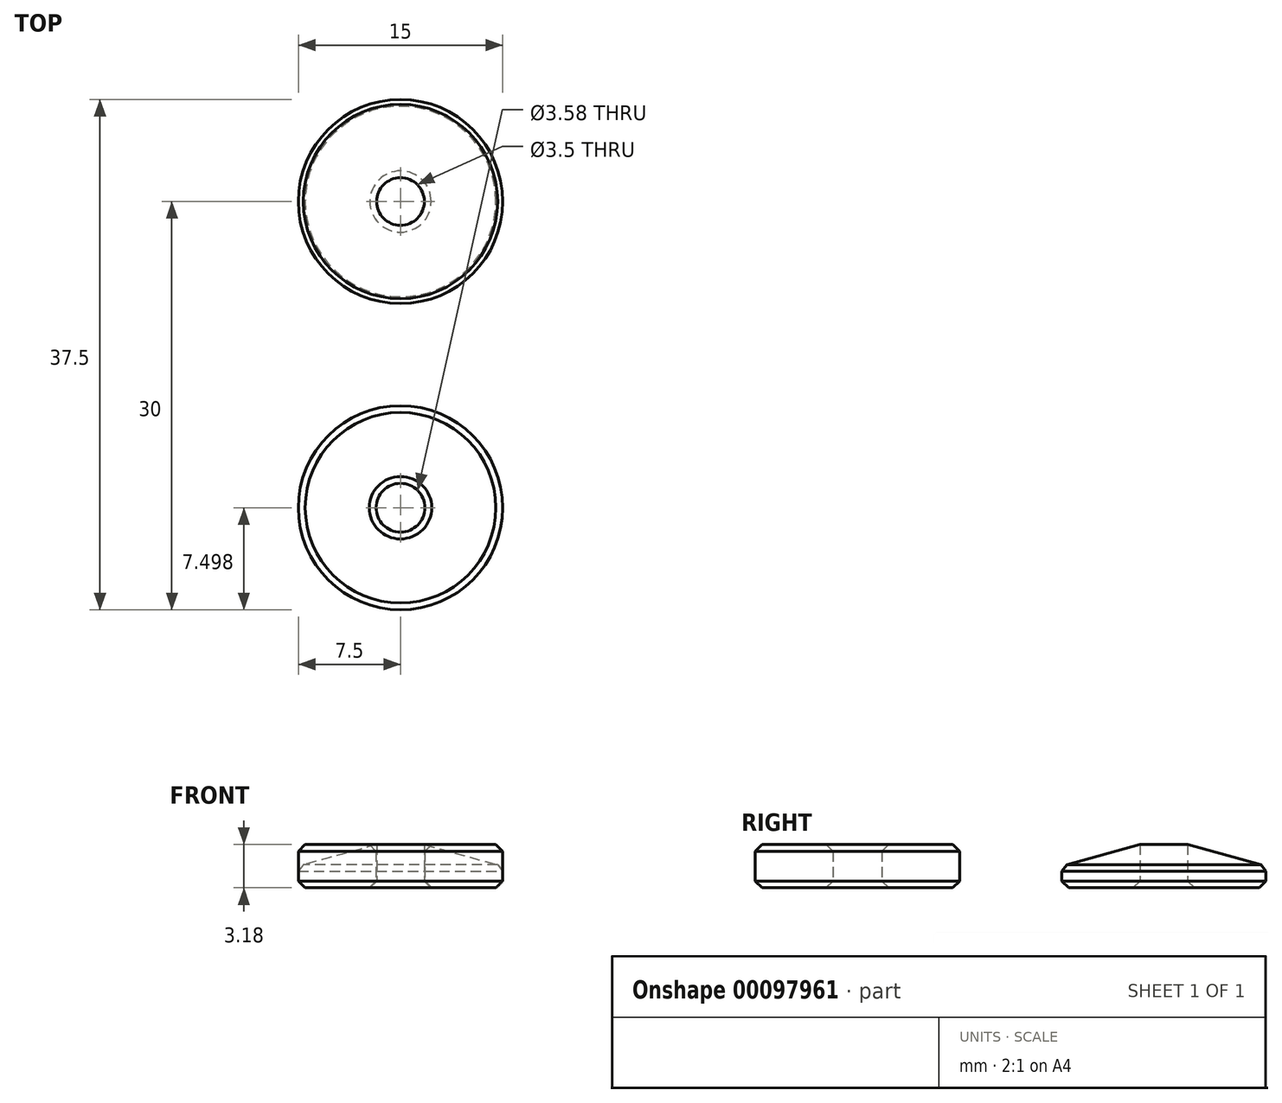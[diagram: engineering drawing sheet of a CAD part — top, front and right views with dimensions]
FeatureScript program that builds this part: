
annotation { "Feature Type Name" : "Feature", "Feature Type Description" : "" }
export const myFeature = defineFeature(function(context is Context, id is Id, definition is map)
    precondition{}
    {
        {
            var Q0;
            Q0=qCreatedBy(makeId("Top.planeOp"),FACE);
            var sketch = newSketch(context, id + "F0", { "sketchPlane" : qUnion([Q0])});
            skCircle(sketch, "E0", {"center": v(0, 0) * mm, "radius": 1.75 * mm});
            skCircle(sketch, "E1", {"center": v(0, 0) * mm, "radius": 7.5 * mm});
            skLineSegment(sketch, "E2", {"start": v(0, 0) * mm, "end": v(0, -22.5) * mm, "construction": true});
            skCircle(sketch, "E3", {"center": v(0, -22.5) * mm, "radius": 7.5 * mm});
            skCircle(sketch, "E4", {"center": v(0, -22.5) * mm, "radius": 1.8 * mm});
            skSolve(sketch);
        }
        {
            var Q0;
            Q0=makeQuery(id+"F0.imprint","IMPRINT",FACE,{"disambiguationData":[TD([[makeQuery(id+"F0.imprint","IMPRINT",EDGE,{"derivedFrom":sQuery(id+"F0.wireOp",EDGE,"E0")}),-1.0]])]});
            extrude(context, id + "F1", {"entities" : qUnion([Q0]), "depth" : 1.59 * mm});
        }
        {
            var Q0;
            Q0=qCreatedBy(makeId("Right.planeOp"),FACE);
            var sketch = newSketch(context, id + "F2", { "sketchPlane" : qUnion([Q0])});
            skLineSegment(sketch, "E5", {"start": v(0, 2.18) * mm, "end": v(0, 3.18) * mm, "construction": true});
            skLineSegment(sketch, "E6", {"start": v(1.75, 1.59) * mm, "end": v(1.75, 3.18) * mm});
            skLineSegment(sketch, "E7", {"start": v(1.75, 3.18) * mm, "end": v(7.5, 1.59) * mm});
            skLineSegment(sketch, "E8", {"start": v(7.5, 1.59) * mm, "end": v(1.75, 1.59) * mm});
            skSolve(sketch);
        }
        {
            var Q0;
            Q0=makeQuery(id+"F2.imprint","IMPRINT",FACE,{"disambiguationData":[TD([[makeQuery(id+"F2.imprint","IMPRINT",EDGE,{"derivedFrom":sQuery(id+"F2.wireOp",EDGE,"E6")}),-1.0]])]});
            var Q1;
            Q1=sQuery(id+"F2.wireOp",EDGE,"E5");
            revolve(context, id + "F3", {"operationType" : NewBodyOperationType.ADD, "entities" : qUnion([Q0]), "axis" : qUnion([Q1]), "revolveType" : RevolveType.FULL});
        }
        {
            var Q0;
            Q0=makeQuery(id+"F0.imprint","IMPRINT",FACE,{"disambiguationData":[TD([[makeQuery(id+"F0.imprint","IMPRINT",EDGE,{"derivedFrom":sQuery(id+"F0.wireOp",EDGE,"E3")}),1.0]])]});
            extrude(context, id + "F4", {"entities" : qUnion([Q0]), "depth" : 3.17 * mm});
        }
        {
            var Q0;
            Q0=makeQuery(id+"F1.opExtrude","CAP_EDGE",EDGE,{"disambiguationData":[OSD([sQuery(id+"F0.wireOp",EDGE,"E1")])],"isStart":true});
            var Q1;
            Q1=makeQuery(id+"F1.opExtrude","CAP_EDGE",EDGE,{"disambiguationData":[OSD([sQuery(id+"F0.wireOp",EDGE,"E0")])],"isStart":true});
            var Q2;
            Q2=makeQuery(id+"F4.opExtrude","CAP_EDGE",EDGE,{"disambiguationData":[OSD([sQuery(id+"F0.wireOp",EDGE,"E3")])],"isStart":false});
            var Q3;
            Q3=makeQuery(id+"F4.opExtrude","CAP_EDGE",EDGE,{"disambiguationData":[OSD([sQuery(id+"F0.wireOp",EDGE,"E3")])],"isStart":true});
            var Q4;
            Q4=makeQuery(id+"F4.opExtrude","CAP_EDGE",EDGE,{"disambiguationData":[OSD([sQuery(id+"F0.wireOp",EDGE,"E4")])],"isStart":false});
            var Q5;
            Q5=makeQuery(id+"F4.opExtrude","CAP_EDGE",EDGE,{"disambiguationData":[OSD([sQuery(id+"F0.wireOp",EDGE,"E4")])],"isStart":true});
            var Q6;
            Q6=makeQuery(id+"F3.boolean.opBoolean","MERGE",EDGE,{"derivedFrom":[makeQuery(id+"F1.opExtrude","CAP_EDGE",EDGE,{"disambiguationData":[OSD([sQuery(id+"F0.wireOp",EDGE,"E1")])],"isStart":false}),makeQuery(id+"F3.opRevolve","SWEPT_EDGE",EDGE,{"disambiguationData":[OSD([sQuery(id+"F2.wireOp",EDGE,"E7"),sQuery(id+"F2.wireOp",EDGE,"E8")])]})]});
            chamfer(context, id + "F5", {"entities" : qUnion([Q0, Q1, Q2, Q3, Q4, Q5, Q6]), "width" : .5 * mm, "tangentPropagation" : true});
        }
    });
